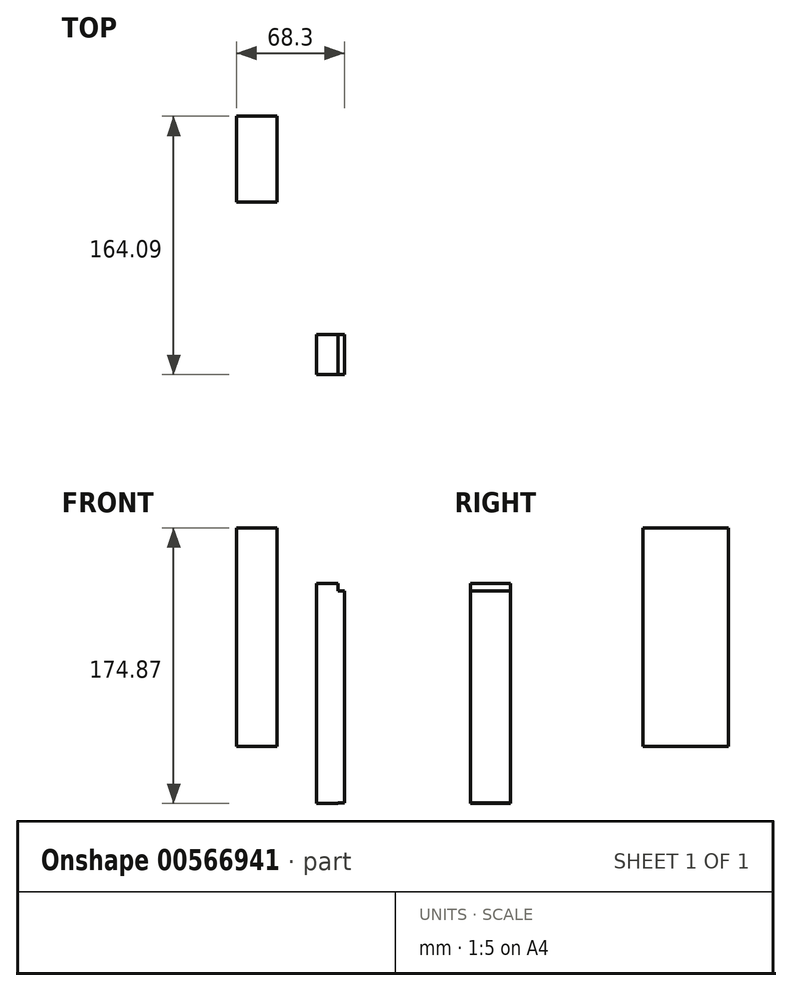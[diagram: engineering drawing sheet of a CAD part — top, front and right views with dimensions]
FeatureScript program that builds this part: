
annotation { "Feature Type Name" : "Feature", "Feature Type Description" : "" }
export const myFeature = defineFeature(function(context is Context, id is Id, definition is map)
    precondition{}
    {
        {
            var Q0;
            Q0=qCreatedBy(makeId("Right.planeOp"),FACE);
            var sketch = newSketch(context, id + "F0", { "sketchPlane" : qUnion([Q0])});
            skLineSegment(sketch, "E0.bottom", {"start": v(138.69, 108.28) * mm, "end": v(84.27, 108.28) * mm});
            skLineSegment(sketch, "E0.top", {"start": v(138.69, -30.34) * mm, "end": v(84.27, -30.34) * mm});
            skLineSegment(sketch, "E0.left", {"start": v(138.69, 108.28) * mm, "end": v(138.69, -30.34) * mm});
            skLineSegment(sketch, "E0.right", {"start": v(84.27, 108.28) * mm, "end": v(84.27, -30.34) * mm});
            skSolve(sketch);
        }
        {
            var Q0;
            Q0 = qSketchRegion(id + "F0", true);
            extrude(context, id + "F1", {"entities" : qUnion([Q0]), "oppositeDirection" : true, "depth" : 25.4 * mm, "offsetDistance" : 25.4 * mm});
        }
        {
            var Q0;
            Q0=qCreatedBy(makeId("Front.planeOp"),FACE);
            var sketch = newSketch(context, id + "F2", { "sketchPlane" : qUnion([Q0])});
            skLineSegment(sketch, "E1.bottom", {"start": v(30.35, 68.19) * mm, "end": v(42.9, 68.19) * mm});
            skLineSegment(sketch, "E1.top", {"start": v(30.35, -66.28) * mm, "end": v(42.9, -66.28) * mm});
            skLineSegment(sketch, "E1.left", {"start": v(30.35, 68.19) * mm, "end": v(30.35, -66.28) * mm});
            skLineSegment(sketch, "E1.right", {"start": v(42.9, 68.19) * mm, "end": v(42.9, -66.28) * mm});
            skSolve(sketch);
        }
        {
            var Q0;
            Q0=makeQuery(id+"F2.imprint","IMPRINT",FACE,{"disambiguationData":[TD([[makeQuery(id+"F2.imprint","IMPRINT",EDGE,{"derivedFrom":sQuery(id+"F2.wireOp",EDGE,"E1.bottom")}),-1.0]])]});
            extrude(context, id + "F3", {"entities" : qUnion([Q0]), "depth" : 25.4 * mm, "offsetDistance" : 25.4 * mm});
        }
        {
            var Q0;
            Q0=qCreatedBy(makeId("Front.planeOp"),FACE);
            var sketch = newSketch(context, id + "F4", { "sketchPlane" : qUnion([Q0])});
            skLineSegment(sketch, "E2.bottom", {"start": v(39, 72.96) * mm, "end": v(25.38, 72.96) * mm});
            skLineSegment(sketch, "E2.top", {"start": v(39, -66.59) * mm, "end": v(25.38, -66.59) * mm});
            skLineSegment(sketch, "E2.left", {"start": v(39, 72.96) * mm, "end": v(39, -66.59) * mm});
            skLineSegment(sketch, "E2.right", {"start": v(25.38, 72.96) * mm, "end": v(25.38, -66.59) * mm});
            skSolve(sketch);
        }
        {
            var Q0;
            Q0 = qSketchRegion(id + "F4", true);
            extrude(context, id + "F5", {"entities" : qUnion([Q0]), "operationType" : NewBodyOperationType.ADD, "depth" : 25.4 * mm, "offsetDistance" : 25.4 * mm});
        }
    });
